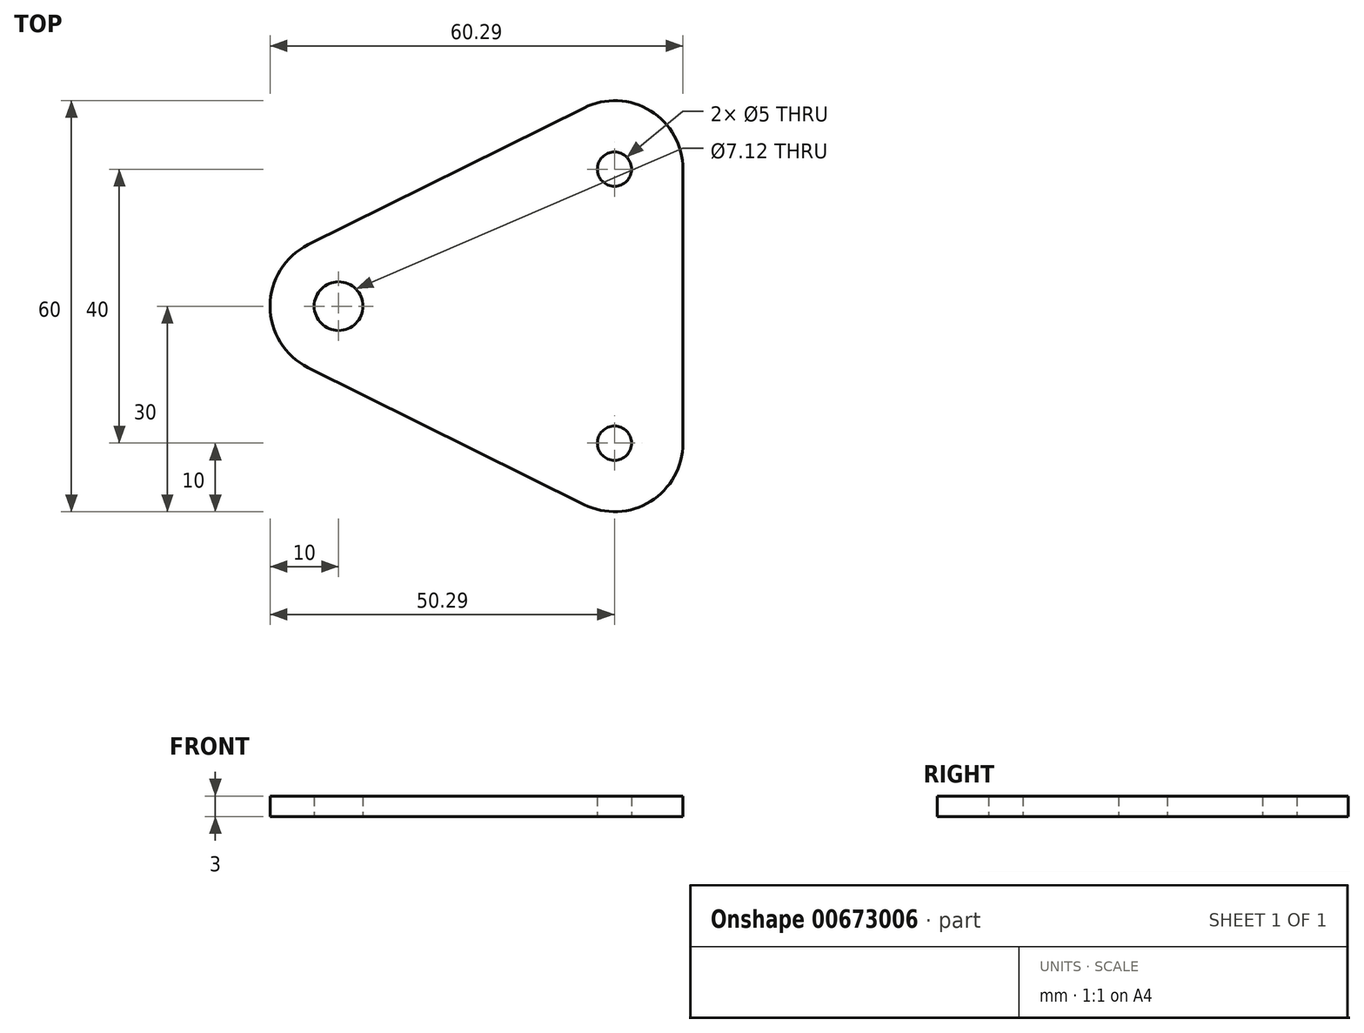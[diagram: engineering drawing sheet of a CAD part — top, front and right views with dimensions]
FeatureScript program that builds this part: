
annotation { "Feature Type Name" : "Feature", "Feature Type Description" : "" }
export const myFeature = defineFeature(function(context is Context, id is Id, definition is map)
    precondition{}
    {
        {
            var Q0;
            Q0=qCreatedBy(makeId("Top.planeOp"),FACE);
            var sketch = newSketch(context, id + "F0", { "sketchPlane" : qUnion([Q0])});
            skCircle(sketch, "E0", {"center": v(0, 0) * mm, "radius": 2.5 * mm});
            skCircle(sketch, "E1", {"center": v(0, 40) * mm, "radius": 2.5 * mm});
            skLineSegment(sketch, "E2", {"start": v(0, 40) * mm, "end": v(0, 0) * mm, "construction": true});
            skLineSegment(sketch, "E3", {"start": v(0, 20) * mm, "end": v(-40.3, 20) * mm, "construction": true});
            skCircle(sketch, "E4", {"center": v(-40.3, 20) * mm, "radius": 3.56 * mm});
            skArc(sketch, "E5", {"start": v(10, 40) * mm, "mid": v(5.27, 48.5) * mm, "end": v(-4.45, 48.96) * mm});
            skArc(sketch, "E6", {"start": v(-4.45, -8.96) * mm, "mid": v(5.27, -8.5) * mm, "end": v(10, 0) * mm});
            skArc(sketch, "E7", {"start": v(-44.74, 28.96) * mm, "mid": v(-50.3, 20) * mm, "end": v(-44.74, 11.04) * mm});
            skLineSegment(sketch, "E8", {"start": v(-44.74, 28.96) * mm, "end": v(-4.45, 48.96) * mm});
            skLineSegment(sketch, "E9", {"start": v(-44.74, 11.04) * mm, "end": v(-4.45, -8.96) * mm});
            skLineSegment(sketch, "E10", {"start": v(10, 0) * mm, "end": v(10, 40) * mm});
            skSolve(sketch);
        }
        {
            var Q0;
            Q0=makeQuery(id+"F0.imprint","IMPRINT",FACE,{"disambiguationData":[TD([[makeQuery(id+"F0.imprint","IMPRINT",EDGE,{"derivedFrom":sQuery(id+"F0.wireOp",EDGE,"E0")}),-1.0]])]});
            extrude(context, id + "F1", {"entities" : qUnion([Q0]), "depth" : 3 * mm, "offsetDistance" : 25 * mm});
        }
    });
